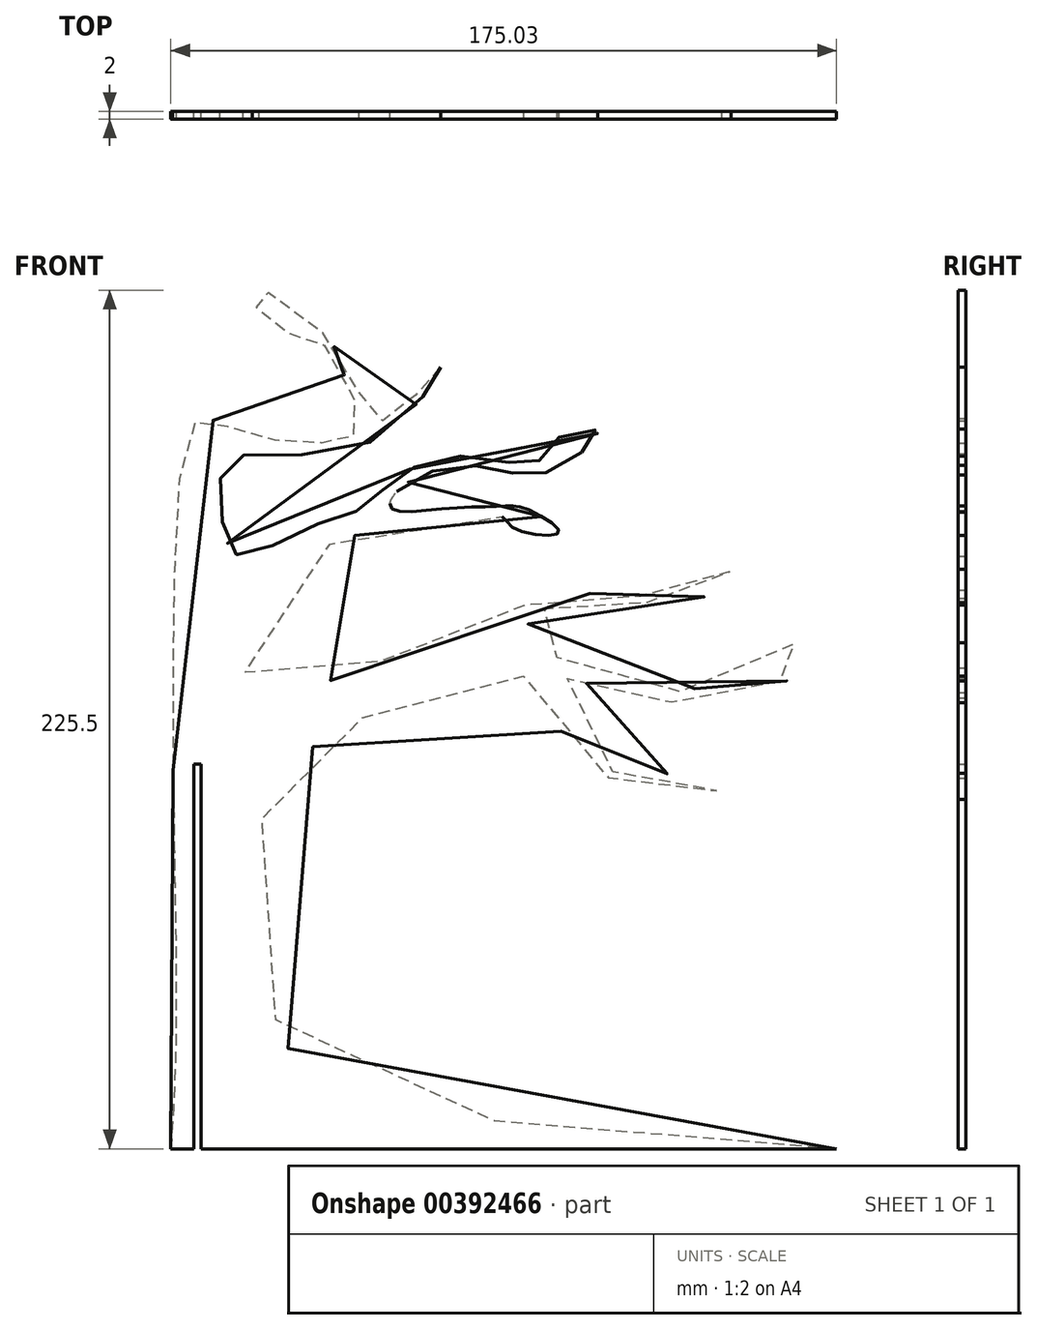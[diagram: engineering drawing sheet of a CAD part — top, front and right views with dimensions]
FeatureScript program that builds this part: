
annotation { "Feature Type Name" : "Feature", "Feature Type Description" : "" }
export const myFeature = defineFeature(function(context is Context, id is Id, definition is map)
    precondition{}
    {
        {
            var Q0;
            Q0=qCreatedBy(makeId("Front.planeOp"),FACE);
            var sketch = newSketch(context, id + "F0", { "sketchPlane" : qUnion([Q0])});
            skFitSpline(sketch, "E0", {"points": [v(168, 25) * mm, v(38.83, 38.41) * mm, v(17.34, 77.48) * mm, v(18.68, 118.47) * mm, v(32.4, 131.83) * mm, v(73.1, 150.8) * mm, v(88.86, 146.42) * mm, v(99.86, 128.37) * mm, v(124.82, 117.6) * mm, v(137.9, 117.73) * mm, v(122.23, 123.57) * mm, v(114.12, 122.31) * mm, v(101.77, 130.83) * mm, v(94.88, 147.46) * mm, v(100.8, 147.8) * mm, v(111.72, 143.38) * mm, v(130.41, 143.48) * mm, v(146.49, 149.1) * mm, v(155.94, 148.03) * mm, v(168, 156) * mm, v(154.46, 157.18) * mm, v(145.58, 152.3) * mm, v(120.91, 144.85) * mm, v(100.37, 152.63) * mm, v(91.39, 154.56) * mm, v(86.11, 157.66) * mm, v(87.27, 163.36) * mm, v(96.36, 168.7) * mm, v(110.18, 167.88) * mm, v(121.03, 168.74) * mm, v(131.12, 169.04) * mm, v(140.18, 176.21) * mm, v(129.25, 175.93) * mm, v(122.41, 172.19) * mm, v(109.4, 169.73) * mm, v(94.69, 171.52) * mm, v(73.07, 160.07) * mm, v(44.51, 151.8) * mm, v(16.08, 144.34) * mm, v(14.72, 167.56) * mm, v(44, 186.93) * mm, v(79.39, 191.45) * mm, v(83.68, 187.78) * mm, v(95.02, 186.92) * mm, v(86.44, 193.1) * mm, v(80.78, 193.81) * mm, v(64.97, 193.13) * mm, v(50.87, 193.38) * mm, v(54.63, 199.6) * mm, v(72.35, 204.44) * mm, v(85.42, 202.09) * mm, v(97.28, 205.24) * mm, v(105.01, 213.5) * mm, v(93.53, 210.83) * mm, v(88.93, 205.01) * mm, v(72.57, 206.9) * mm, v(52.62, 201.53) * mm, v(43.43, 193.43) * mm, v(28.01, 187.7) * mm, v(10.67, 180.9) * mm, v(6.14, 193.55) * mm, v(9.14, 206.32) * mm, v(44.57, 210.22) * mm, v(64, 230.24) * mm, v(56.87, 222.47) * mm, v(47.33, 216.35) * mm, v(35.06, 236.84) * mm, v(14.66, 250) * mm, v(20.8, 240.14) * mm, v(31.07, 238.06) * mm, v(42.47, 215.81) * mm, v(39.5, 211.5) * mm, v(29, 210.42) * mm, v(10.25, 213.65) * mm, v(0, 216.34) * mm, v(-6.16, 173.56) * mm, v(-6.14, 107.23) * mm, v(-5.93, 41.33) * mm, v(-7, 25) * mm], "startDerivative": vector(-2322, 1083.15) * mm, "endDerivative": vector(17.28, -1035.86) * mm});
            skLineSegment(sketch, "E1", {"start": v(168, 25) * mm, "end": v(-7, 25) * mm});
            skSolve(sketch);
        }
        {
            var Q0;
            Q0 = qSketchRegion(id + "F0", true);
            extrude(context, id + "F1", {"entities" : qUnion([Q0]), "depth" : 2 * mm});
        }
        {
            var Q0;
            Q0=qCreatedBy(makeId("Front.planeOp"),FACE);
            var sketch = newSketch(context, id + "F2", { "sketchPlane" : qUnion([Q0])});
            skLineSegment(sketch, "E2.bottom", {"start": v(1, 0) * mm, "end": v(-1, 0) * mm});
            skLineSegment(sketch, "E2.top", {"start": v(1, 126) * mm, "end": v(-1, 126) * mm});
            skLineSegment(sketch, "E2.left", {"start": v(1, 0) * mm, "end": v(1, 126) * mm});
            skLineSegment(sketch, "E2.right", {"start": v(-1, 0) * mm, "end": v(-1, 126) * mm});
            skSolve(sketch);
        }
        {
            var Q0;
            Q0 = qSketchRegion(id + "F2", true);
            extrude(context, id + "F3", {"entities" : qUnion([Q0]), "operationType" : NewBodyOperationType.REMOVE, "depth" : 25 * mm});
        }
    });
